# Revit family: Sliding_Barn_Style_Double_Door_14548
name_source: partatom
category: Doors
revit_build: Autodesk Revit 2017 (Build: 20160606_1515(x64)
units: mm (PartAtom-declared; Revit-internal decimal feet)

## family parameters
Always vertical = Yes
Cut with Voids When Loaded = No
Host = Wall
OmniClass Number = 23.30.10.00
OmniClass Title = Doors
Room Calculation Point = No
Shared = No

## types (6) — shared parameters
Function = Interior
Wall Closure = By host

## per-type parameters (varying)
| type | Door Panel Width | Height | Rough Height | Rough Width | Track Width | Width |
| (2)2'-0" x 6'-8" | 2' - 0" | 6' - 8" | 6' - 9 1/4" | 8' - 0" | 8' - 2" | 4' - 0" |
| (2)2'-6" x 7'-0" | 2' - 6" | 7' - 0" | 7' - 1 1/4" | 10' - 0" | 10' - 2" | 5' - 0" |
| (2)2'-0" x 7'-0" | 2' - 0" | 7' - 0" | 7' - 1 1/4" | 8' - 0" | 8' - 2" | 4' - 0" |
| (2)2'-6" x 6'-8" | 3' - 0" | 7' - 0" | 7' - 1 1/4" | 12' - 0" | 12' - 2" | 6' - 0" |
| (2)3'-0" x 6'-8" | 3' - 0" | 6' - 8" | 6' - 9 1/4" | 12' - 0" | 12' - 2" | 6' - 0" |
| (2)3'-0" x 7'-0" | 3' - 0" | 7' - 0" | 7' - 1 1/4" | 12' - 0" | 12' - 2" | 6' - 0" |

## geometry (parser evidence)
native form markers: Sweep x2
no freeform markers — native parametric forms only
